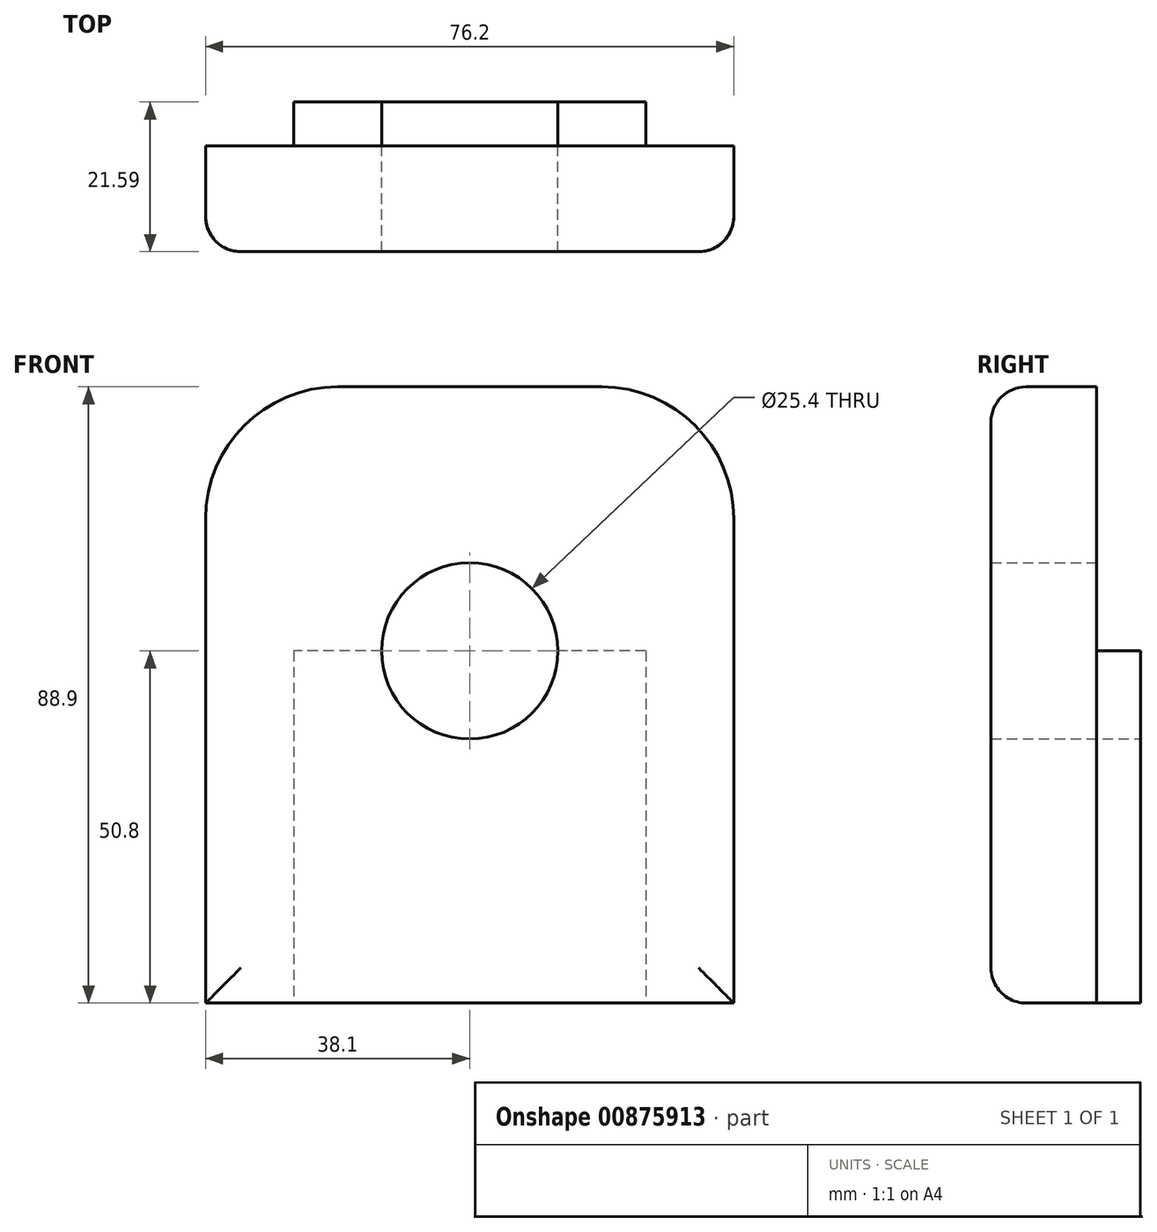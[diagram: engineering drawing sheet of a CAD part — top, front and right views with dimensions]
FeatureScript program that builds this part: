
annotation { "Feature Type Name" : "Feature", "Feature Type Description" : "" }
export const myFeature = defineFeature(function(context is Context, id is Id, definition is map)
    precondition{}
    {
        {
            var Q0;
            Q0=qCreatedBy(makeId("Front.planeOp"),FACE);
            var sketch = newSketch(context, id + "F0", { "sketchPlane" : qUnion([Q0])});
            skLineSegment(sketch, "E0.bottom", {"start": v(-19.05, 38.1) * mm, "end": v(19.05, 38.1) * mm});
            skLineSegment(sketch, "E0.top", {"start": v(-38.1, -50.8) * mm, "end": v(38.1, -50.8) * mm});
            skLineSegment(sketch, "E0.left", {"start": v(-38.1, 19.05) * mm, "end": v(-38.1, -50.8) * mm});
            skLineSegment(sketch, "E0.right", {"start": v(38.1, 19.05) * mm, "end": v(38.1, -50.8) * mm});
            skArc(sketch, "E1", {"start": v(12.7, 0) * mm, "mid": v(0, 12.7) * mm, "end": v(-12.7, 0) * mm, "construction": true});
            skLineSegment(sketch, "E2.bottom", {"start": v(12.7, 0) * mm, "end": v(12.7, 0) * mm});
            skLineSegment(sketch, "E2.top", {"start": v(-12.7, -50.8) * mm, "end": v(12.7, -50.8) * mm, "construction": true});
            skLineSegment(sketch, "E2.left", {"start": v(-12.7, 0) * mm, "end": v(-12.7, -50.8) * mm, "construction": true});
            skLineSegment(sketch, "E2.right", {"start": v(12.7, 0) * mm, "end": v(12.7, -50.8) * mm, "construction": true});
            skCircle(sketch, "E3", {"center": v(0, 0) * mm, "radius": 12.7 * mm});
            skPoint(sketch, "E4.visualSharp", {"position": v(-38.1, 38.1) * mm});
            skArc(sketch, "E4.filletArc", {"start": v(-19.05, 38.1) * mm, "mid": v(-32.52, 32.52) * mm, "end": v(-38.1, 19.05) * mm});
            skPoint(sketch, "E5.visualSharp", {"position": v(38.1, 38.1) * mm});
            skArc(sketch, "E5.filletArc", {"start": v(38.1, 19.05) * mm, "mid": v(32.52, 32.52) * mm, "end": v(19.05, 38.1) * mm});
            skSolve(sketch);
        }
        {
            var Q0;
            Q0=makeQuery(id+"F0.imprint","IMPRINT",FACE,{"disambiguationData":[TD([[makeQuery(id+"F0.imprint","IMPRINT",EDGE,{"derivedFrom":sQuery(id+"F0.wireOp",EDGE,"E0.bottom")}),-1.0]])]});
            extrude(context, id + "F1", {"entities" : qUnion([Q0]), "depth" : 15.24 * mm});
        }
        {
            var Q0;
            Q0=qCreatedBy(makeId("Front.planeOp"),FACE);
            var sketch = newSketch(context, id + "F2", { "sketchPlane" : qUnion([Q0])});
            skPoint(sketch, "E6.orphan", {"position": v(12.7, 0) * mm});
            skPoint(sketch, "E7.orphan", {"position": v(-12.7, 0) * mm});
            skPoint(sketch, "E8.0.end.orphan", {"position": v(12.7, -50.8) * mm});
            skPoint(sketch, "E9.0.end.orphan", {"position": v(-12.7, -50.8) * mm});
            skLineSegment(sketch, "E10.bottom", {"start": v(25.4, 0) * mm, "end": v(12.7, 0) * mm});
            skLineSegment(sketch, "E10.top", {"start": v(25.4, -50.8) * mm, "end": v(-25.4, -50.8) * mm});
            skLineSegment(sketch, "E10.left", {"start": v(25.4, 0) * mm, "end": v(25.4, -50.8) * mm});
            skLineSegment(sketch, "E10.right", {"start": v(-25.4, 0) * mm, "end": v(-25.4, -50.8) * mm});
            skArc(sketch, "E11.0", {"start": v(-12.7, 0) * mm, "mid": v(0, -12.7) * mm, "end": v(12.7, 0) * mm});
            skLineSegment(sketch, "E12.trimOffspring", {"start": v(-12.7, 0) * mm, "end": v(-25.4, 0) * mm});
            skSolve(sketch);
        }
        {
            var Q0;
            Q0=qSketchRegion(id+"F2",true);
            extrude(context, id + "F3", {"entities" : qUnion([Q0]), "operationType" : NewBodyOperationType.ADD, "oppositeDirection" : true, "depth" : 6.35 * mm});
        }
        {
            var Q0;
            Q0=makeQuery(id+"F1.opExtrude","CAP_EDGE",EDGE,{"disambiguationData":[OSD([sQuery(id+"F0.wireOp",EDGE,"E0.left")])],"isStart":false});
            var Q1;
            Q1=makeQuery(id+"F1.opExtrude","CAP_EDGE",EDGE,{"disambiguationData":[OSD([sQuery(id+"F0.wireOp",EDGE,"E4.filletArc")])],"isStart":false});
            var Q2;
            Q2=makeQuery(id+"F1.opExtrude","CAP_EDGE",EDGE,{"disambiguationData":[OSD([sQuery(id+"F0.wireOp",EDGE,"E0.bottom")])],"isStart":false});
            var Q3;
            Q3=makeQuery(id+"F1.opExtrude","CAP_EDGE",EDGE,{"disambiguationData":[OSD([sQuery(id+"F0.wireOp",EDGE,"E5.filletArc")])],"isStart":false});
            var Q4;
            Q4=makeQuery(id+"F1.opExtrude","CAP_EDGE",EDGE,{"disambiguationData":[OSD([sQuery(id+"F0.wireOp",EDGE,"E0.right")])],"isStart":false});
            var Q5;
            Q5=makeQuery(id+"F1.opExtrude","CAP_EDGE",EDGE,{"disambiguationData":[OSD([sQuery(id+"F0.wireOp",EDGE,"E0.top")])],"isStart":false});
            fillet(context, id + "F4", {"entities" : qUnion([Q0, Q1, Q2, Q3, Q4, Q5]), "radius" : 5.08 * mm, "tangentPropagation" : true, "allowEdgeOverflow" : false});
        }
    });
